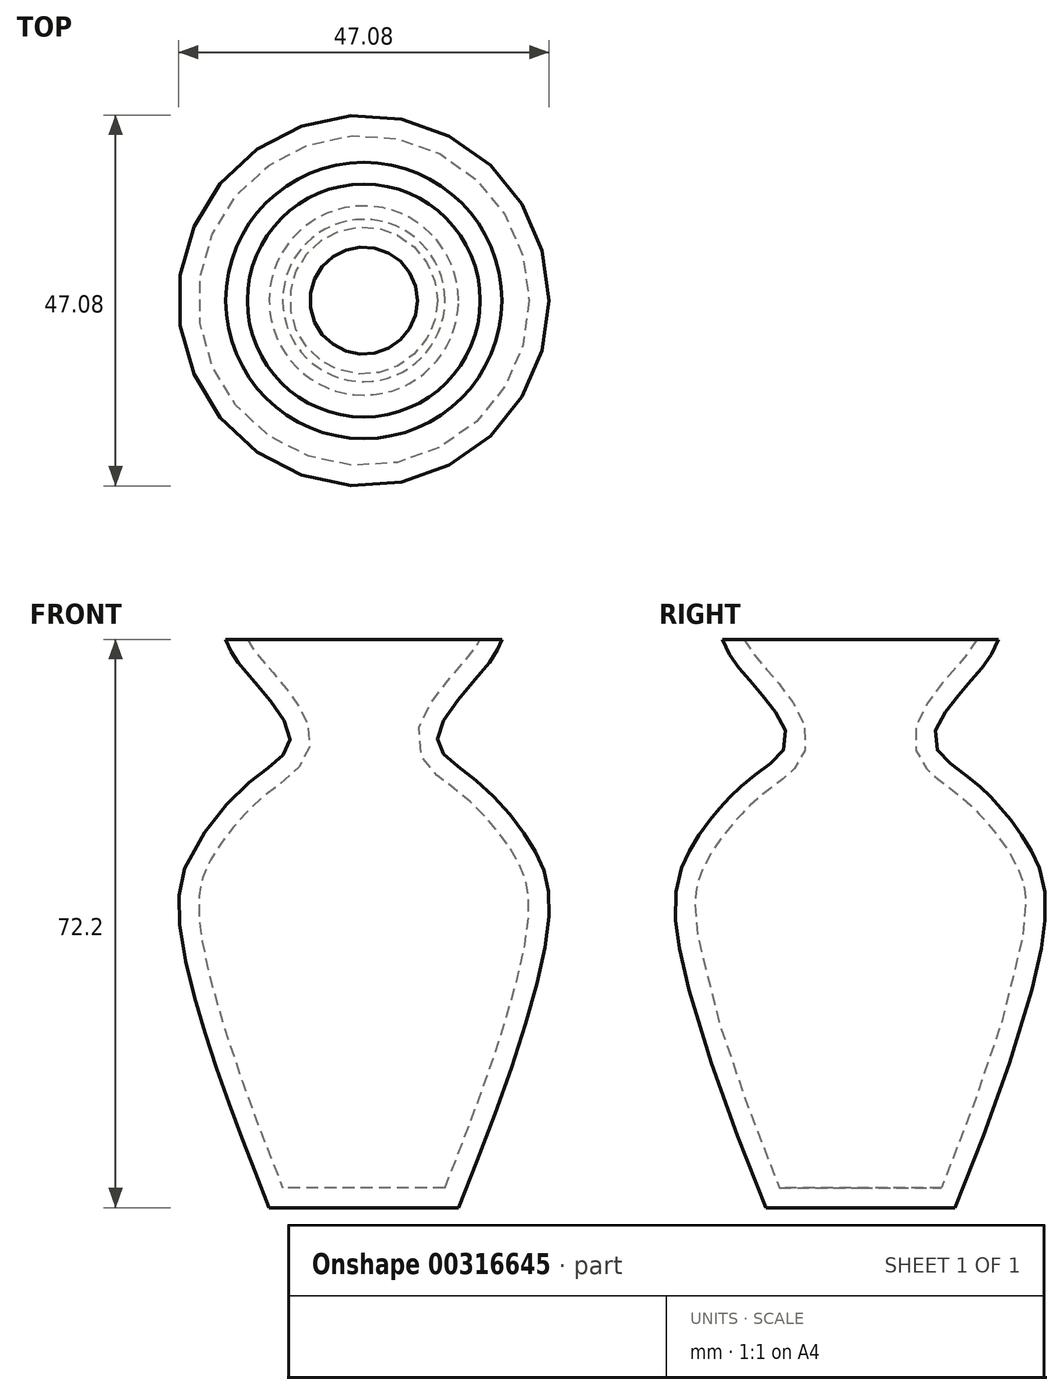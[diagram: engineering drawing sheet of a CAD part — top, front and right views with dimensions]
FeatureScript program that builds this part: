
annotation { "Feature Type Name" : "Feature", "Feature Type Description" : "" }
export const myFeature = defineFeature(function(context is Context, id is Id, definition is map)
    precondition{}
    {
        {
            var Q0;
            Q0=qCreatedBy(makeId("Front.planeOp"),FACE);
            var sketch = newSketch(context, id + "F0", { "sketchPlane" : qUnion([Q0])});
            skLineSegment(sketch, "E0", {"start": v(0, 0) * mm, "end": v(0, 93.42) * mm, "construction": true});
            skLineSegment(sketch, "E1", {"start": v(0, 0) * mm, "end": v(-12.02, 0) * mm});
            skFitSpline(sketch, "E2", {"points": [v(-12.02, 0) * mm, v(-23.48, 36.79) * mm, v(-21.23, 46.2) * mm, v(-13.86, 54.6) * mm, v(-9.36, 59.71) * mm, v(-15.7, 68.92) * mm, v(-17.55, 72.2) * mm], "startDerivative": vector(-55.43, 136.5) * mm, "endDerivative": vector(-11.28, 28.97) * mm});
            skLineSegment(sketch, "E3", {"start": v(-17.55, 72.2) * mm, "end": v(0, 72.2) * mm});
            skLineSegment(sketch, "E4", {"start": v(0, 72.2) * mm, "end": v(0, 0) * mm});
            skSolve(sketch);
        }
        {
            var Q0;
            Q0=makeQuery(id+"F0.imprint","IMPRINT",FACE,{"disambiguationData":[TD([[makeQuery(id+"F0.imprint","IMPRINT",EDGE,{"derivedFrom":sQuery(id+"F0.wireOp",EDGE,"E1")}),-1.0]])]});
            var Q1;
            Q1=sQuery(id+"F0.wireOp",EDGE,"E4");
            revolve(context, id + "F1", {"entities" : qUnion([Q0]), "axis" : qUnion([Q1]), "revolveType" : RevolveType.FULL});
        }
        {
            var Q0;
            Q0=makeQuery(id+"F1.opRevolve","SWEPT_FACE",FACE,{"disambiguationData":[OSD([sQuery(id+"F0.wireOp",EDGE,"E3")])]});
            shell(context, id + "F2", {"entities" : qUnion([Q0]), "thickness" : 2.54 * mm});
        }
    });
